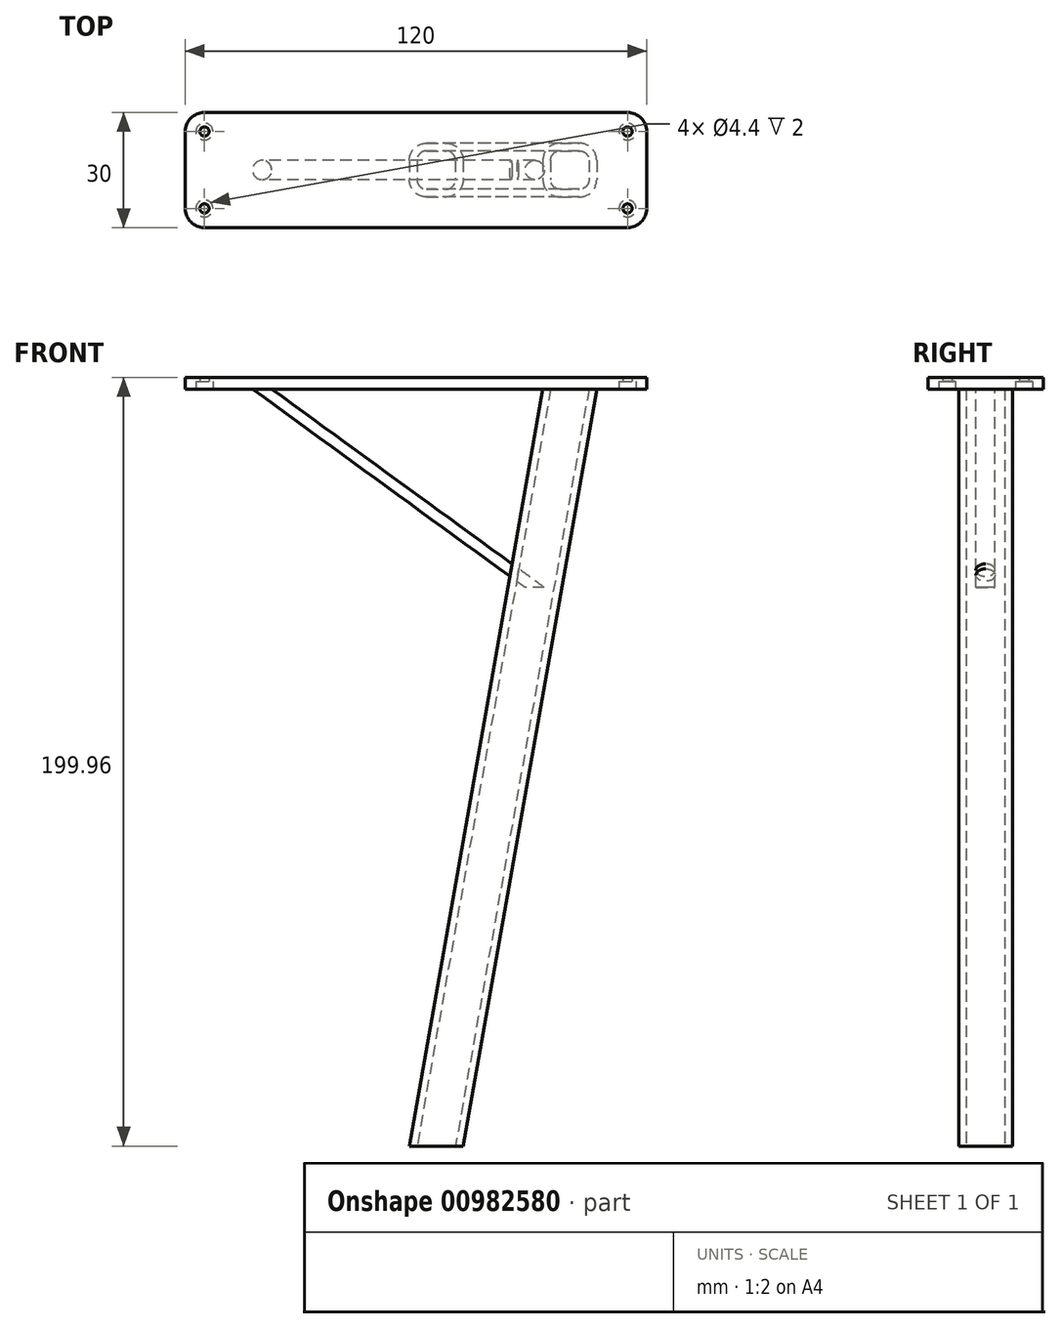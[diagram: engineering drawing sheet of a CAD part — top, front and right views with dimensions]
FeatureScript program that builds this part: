
annotation { "Feature Type Name" : "Feature", "Feature Type Description" : "" }
export const myFeature = defineFeature(function(context is Context, id is Id, definition is map)
    precondition{}
    {
        {
            assignVariable(context, id + "F0", {"name" : "depth", "anyValue" : 3 * mm});
        }
        {
            var Q0;
            Q0=qCreatedBy(makeId("Top.planeOp"),FACE);
            var sketch = newSketch(context, id + "F1", { "sketchPlane" : qUnion([Q0])});
            skLineSegment(sketch, "E0.bottom", {"start": v(55, -15) * mm, "end": v(-55, -15) * mm});
            skLineSegment(sketch, "E0.top", {"start": v(55, 15) * mm, "end": v(-55, 15) * mm});
            skLineSegment(sketch, "E0.left", {"start": v(60, -10) * mm, "end": v(60, 10) * mm});
            skLineSegment(sketch, "E0.right", {"start": v(-60, -10) * mm, "end": v(-60, 10) * mm});
            skPoint(sketch, "E0.middle", {"position": v(0, 0) * mm});
            skPoint(sketch, "E1.visualSharp", {"position": v(60, 15) * mm});
            skArc(sketch, "E1.filletArc", {"start": v(60, 10) * mm, "mid": v(58.54, 13.54) * mm, "end": v(55, 15) * mm});
            skPoint(sketch, "E2.visualSharp", {"position": v(60, -15) * mm});
            skArc(sketch, "E2.filletArc", {"start": v(55, -15) * mm, "mid": v(58.54, -13.54) * mm, "end": v(60, -10) * mm});
            skPoint(sketch, "E3.visualSharp", {"position": v(-60, -15) * mm});
            skArc(sketch, "E3.filletArc", {"start": v(-60, -10) * mm, "mid": v(-58.54, -13.54) * mm, "end": v(-55, -15) * mm});
            skPoint(sketch, "E4.visualSharp", {"position": v(-60, 15) * mm});
            skArc(sketch, "E4.filletArc", {"start": v(-55, 15) * mm, "mid": v(-58.54, 13.54) * mm, "end": v(-60, 10) * mm});
            skPoint(sketch, "E5", {"position": v(40, 0) * mm});
            skLineSegment(sketch, "E6.bottom", {"start": v(37.5, 5) * mm, "end": v(42.5, 5) * mm});
            skLineSegment(sketch, "E6.top", {"start": v(37.5, -5) * mm, "end": v(42.5, -5) * mm});
            skLineSegment(sketch, "E6.left", {"start": v(35, 2.5) * mm, "end": v(35, -2.5) * mm});
            skLineSegment(sketch, "E6.right", {"start": v(45, 2.5) * mm, "end": v(45, -2.5) * mm});
            skPoint(sketch, "E7.visualSharp", {"position": v(45, -5) * mm});
            skArc(sketch, "E7.filletArc", {"start": v(42.5, -5) * mm, "mid": v(44.27, -4.27) * mm, "end": v(45, -2.5) * mm});
            skPoint(sketch, "E8.visualSharp", {"position": v(45, 5) * mm});
            skArc(sketch, "E8.filletArc", {"start": v(45, 2.5) * mm, "mid": v(44.27, 4.27) * mm, "end": v(42.5, 5) * mm});
            skPoint(sketch, "E9.visualSharp", {"position": v(35, 5) * mm});
            skArc(sketch, "E9.filletArc", {"start": v(37.5, 5) * mm, "mid": v(35.73, 4.27) * mm, "end": v(35, 2.5) * mm});
            skPoint(sketch, "E10.visualSharp", {"position": v(35, -5) * mm});
            skArc(sketch, "E10.filletArc", {"start": v(35, -2.5) * mm, "mid": v(35.73, -4.27) * mm, "end": v(37.5, -5) * mm});
            skArc(sketch, "E11.0", {"start": v(47, 2.5) * mm, "mid": v(45.68, 5.68) * mm, "end": v(42.5, 7) * mm});
            skLineSegment(sketch, "E11.1", {"start": v(37.5, 7) * mm, "end": v(42.5, 7) * mm});
            skLineSegment(sketch, "E11.2", {"start": v(47, 2.5) * mm, "end": v(47, -2.5) * mm});
            skArc(sketch, "E11.3", {"start": v(37.5, 7) * mm, "mid": v(34.32, 5.68) * mm, "end": v(33, 2.5) * mm});
            skArc(sketch, "E11.4", {"start": v(42.5, -7) * mm, "mid": v(45.68, -5.68) * mm, "end": v(47, -2.5) * mm});
            skLineSegment(sketch, "E11.5", {"start": v(37.5, -7) * mm, "end": v(42.5, -7) * mm});
            skArc(sketch, "E11.6", {"start": v(33, -2.5) * mm, "mid": v(34.32, -5.68) * mm, "end": v(37.5, -7) * mm});
            skLineSegment(sketch, "E11.7", {"start": v(33, 2.5) * mm, "end": v(33, -2.5) * mm});
            skPoint(sketch, "E12", {"position": v(-40, 0) * mm});
            skCircle(sketch, "E13", {"center": v(-40, 0) * mm, "radius": 2.5 * mm});
            skSolve(sketch);
        }
        {
            var Q0;
            Q0=makeQuery(id+"F1.imprint","IMPRINT",FACE,{"disambiguationData":[TD([[makeQuery(id+"F1.imprint","IMPRINT",EDGE,{"derivedFrom":sQuery(id+"F1.wireOp",EDGE,"E0.bottom")}),-1.0]])]});
            var Q1;
            Q1=makeQuery(id+"F1.imprint","IMPRINT",FACE,{"disambiguationData":[TD([[makeQuery(id+"F1.imprint","IMPRINT",EDGE,{"derivedFrom":sQuery(id+"F1.wireOp",EDGE,"E6.bottom")}),1.0]])]});
            var Q2;
            Q2=makeQuery(id+"F1.imprint","IMPRINT",FACE,{"disambiguationData":[TD([[makeQuery(id+"F1.imprint","IMPRINT",EDGE,{"derivedFrom":sQuery(id+"F1.wireOp",EDGE,"E6.bottom")}),-1.0]])]});
            var Q3;
            Q3=makeQuery(id+"F1.imprint","IMPRINT",FACE,{"disambiguationData":[TD([[makeQuery(id+"F1.imprint","IMPRINT",EDGE,{"derivedFrom":sQuery(id+"F1.wireOp",EDGE,"E13")}),1.0]])]});
            extrude(context, id + "F2", {"entities" : qUnion([Q0, Q1, Q2, Q3]), "depth" : getVariable(context, 'depth'), "offsetDistance" : 25 * mm});
        }
        {
            var Q0;
            Q0=sQuery(id+"F1.wireOp",VERTEX,"E1.filletArc.center");
            var Q1;
            Q1=sQuery(id+"F1.wireOp",VERTEX,"E4.filletArc.center");
            var Q2;
            Q2=sQuery(id+"F1.wireOp",VERTEX,"E3.filletArc.center");
            var Q3;
            Q3=sQuery(id+"F1.wireOp",VERTEX,"E2.filletArc.center");
            var Q4;
            Q4=makeQuery(id+"F2.opExtrude","SWEPT_BODY",BODY,{"disambiguationData":[OSD([sQuery(id+"F1.wireOp",EDGE,"E0.bottom"),sQuery(id+"F1.wireOp",EDGE,"E0.top"),sQuery(id+"F1.wireOp",EDGE,"E0.left"),sQuery(id+"F1.wireOp",EDGE,"E0.right"),sQuery(id+"F1.wireOp",EDGE,"E1.filletArc"),sQuery(id+"F1.wireOp",EDGE,"E2.filletArc"),sQuery(id+"F1.wireOp",EDGE,"E3.filletArc"),sQuery(id+"F1.wireOp",EDGE,"E4.filletArc")])]});
            hole(context, id + "F3", {"style" : HoleStyle.C_BORE, "endStyle" : HoleEndStyle.THROUGH, "oppositeDirection" : true, "standardTappedOrClearance" : lookupTablePath({ "fit" : "Normal", "standard" : "ISO", "size" : "M2", "type" : "Clearance" }), "standardBlindInLast" : lookupTablePath({ "fit" : "Normal", "standard" : "ISO", "engagement" : "75%", "pitch" : "0.25 mm", "size" : "M2", "type" : "Clearance & tapped" }), "holeDiameter" : 2.4 * mm, "cBoreDiameter" : 4.4 * mm, "cBoreDepth" : 2 * mm, "majorDiameter" : 3 * mm, "isTappedThrough" : true, "tappedDepth" : 12 * mm, "tapClearance" : 3, "locations" : qUnion([Q0, Q1, Q2, Q3]), "scope" : qUnion([Q4])});
        }
        {
            var Q0;
            Q0=qCreatedBy(makeId("Front.planeOp"),FACE);
            var sketch = newSketch(context, id + "F4", { "sketchPlane" : qUnion([Q0])});
            skPoint(sketch, "E14.0", {"position": v(40, 0) * mm});
            skLineSegment(sketch, "E15", {"start": v(40, 0) * mm, "end": v(5.27, -196.96) * mm});
            skLineSegment(sketch, "E16.0", {"start": v(55, 0) * mm, "end": v(-55, 0) * mm, "construction": true});
            skLineSegment(sketch, "E17", {"start": v(30.9, -51.62) * mm, "end": v(-40, 0) * mm});
            skSolve(sketch);
        }
        {
            var Q0;
            Q0=makeQuery(id+"F1.imprint","IMPRINT",FACE,{"disambiguationData":[TD([[makeQuery(id+"F1.imprint","IMPRINT",EDGE,{"derivedFrom":sQuery(id+"F1.wireOp",EDGE,"E6.bottom")}),1.0]])]});
            var Q1;
            Q1=sQuery(id+"F4.wireOp",EDGE,"E15");
            sweep(context, id + "F5", {"operationType" : NewBodyOperationType.ADD, "profiles" : qUnion([Q0]), "path" : qUnion([Q1])});
        }
        {
            var Q0;
            Q0=makeQuery(id+"F1.imprint","IMPRINT",FACE,{"disambiguationData":[TD([[makeQuery(id+"F1.imprint","IMPRINT",EDGE,{"derivedFrom":sQuery(id+"F1.wireOp",EDGE,"E13")}),1.0]])]});
            var Q1;
            Q1=sQuery(id+"F4.wireOp",EDGE,"E17");
            sweep(context, id + "F6", {"operationType" : NewBodyOperationType.ADD, "profiles" : qUnion([Q0]), "path" : qUnion([Q1])});
        }
    });
